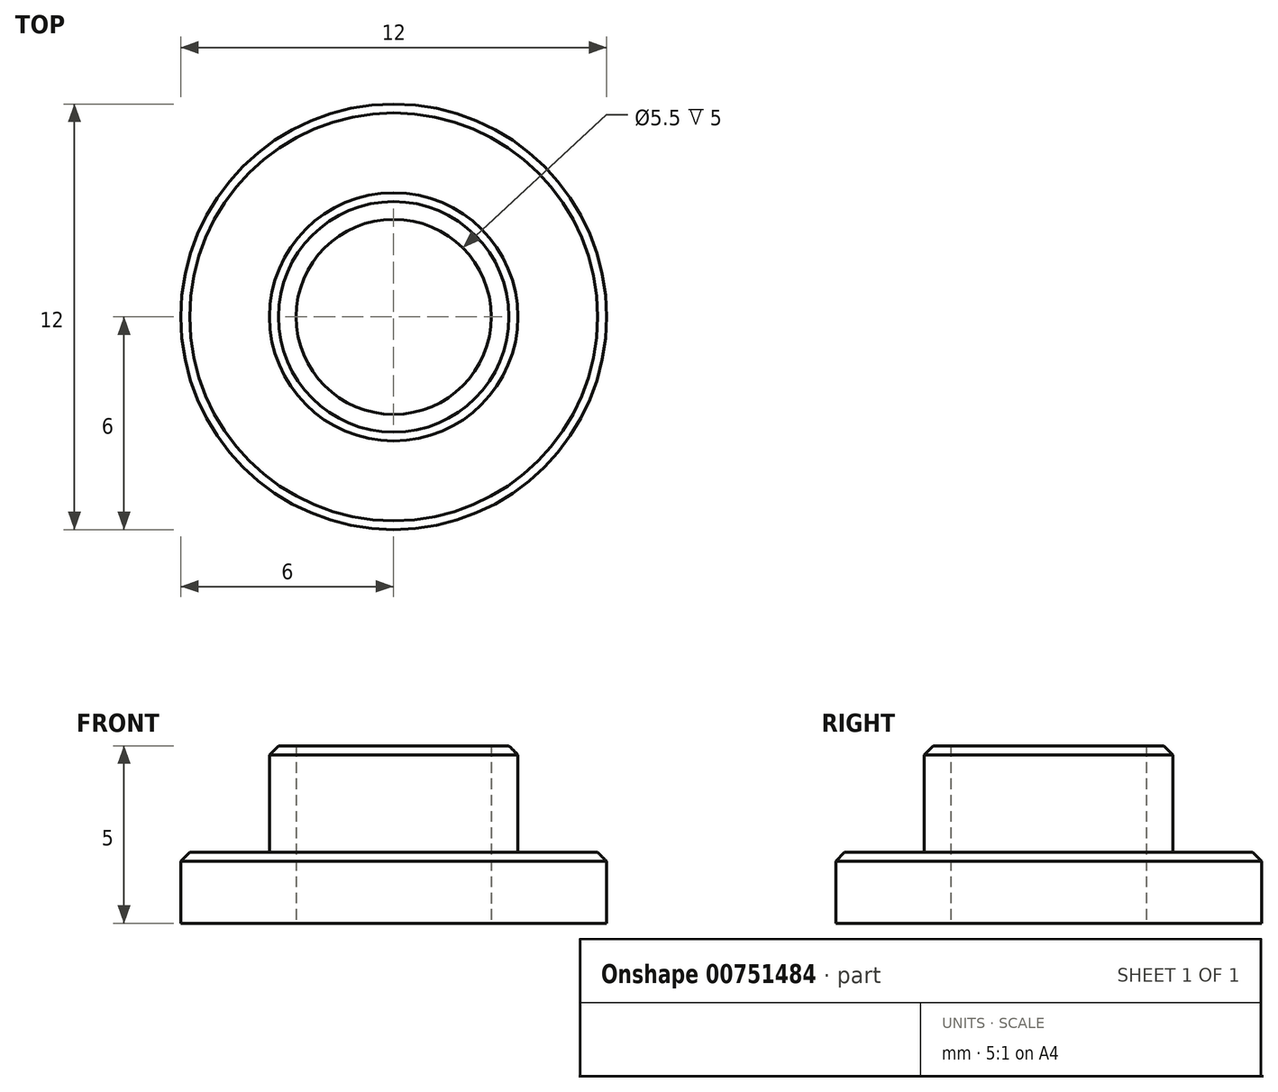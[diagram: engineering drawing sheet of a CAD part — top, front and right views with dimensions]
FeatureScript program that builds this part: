
annotation { "Feature Type Name" : "Feature", "Feature Type Description" : "" }
export const myFeature = defineFeature(function(context is Context, id is Id, definition is map)
    precondition{}
    {
        {
            assignVariable(context, id + "F0", {"name" : "SpacerHeight", "anyValue" : 5});
        }
        {
            var Q0;
            Q0=qCreatedBy(makeId("Top.planeOp"),FACE);
            var sketch = newSketch(context, id + "F1", { "sketchPlane" : qUnion([Q0])});
            skCircle(sketch, "E0", {"center": v(0, 0) * mm, "radius": 2.75 * mm});
            skCircle(sketch, "E1", {"center": v(0, 0) * mm, "radius": 3.5 * mm});
            skCircle(sketch, "E2", {"center": v(0, 0) * mm, "radius": 6 * mm});
            skSolve(sketch);
        }
        {
            var Q0;
            Q0=makeQuery(id+"F1.imprint","IMPRINT",FACE,{"disambiguationData":[TD([[makeQuery(id+"F1.imprint","IMPRINT",EDGE,{"derivedFrom":sQuery(id+"F1.wireOp",EDGE,"E0")}),-1.0]])]});
            extrude(context, id + "F2", {"entities" : qUnion([Q0]), "depth" : (getVariable(context, 'SpacerHeight')) * mm, "offsetDistance" : 25 * mm});
        }
        {
            var Q0;
            Q0=makeQuery(id+"F1.imprint","IMPRINT",FACE,{"disambiguationData":[TD([[makeQuery(id+"F1.imprint","IMPRINT",EDGE,{"derivedFrom":sQuery(id+"F1.wireOp",EDGE,"E1")}),-1.0]])]});
            extrude(context, id + "F3", {"entities" : qUnion([Q0]), "operationType" : NewBodyOperationType.ADD, "depth" : 2 * mm, "offsetDistance" : 25 * mm});
        }
        {
            var Q0;
            Q0=makeQuery(id+"F2.opExtrude","CAP_EDGE",EDGE,{"disambiguationData":[OSD([sQuery(id+"F1.wireOp",EDGE,"E1")])],"isStart":false});
            var Q1;
            Q1=makeQuery(id+"F2.opExtrude","CAP_EDGE",EDGE,{"disambiguationData":[OSD([sQuery(id+"F1.wireOp",EDGE,"E1")])],"isStart":true});
            var Q2;
            Q2=makeQuery(id+"F3.opExtrude","CAP_EDGE",EDGE,{"disambiguationData":[OSD([sQuery(id+"F1.wireOp",EDGE,"E1")])],"isStart":false});
            var Q3;
            Q3=makeQuery(id+"F3.opExtrude","CAP_EDGE",EDGE,{"disambiguationData":[OSD([sQuery(id+"F1.wireOp",EDGE,"E2")])],"isStart":false});
            chamfer(context, id + "F4", {"entities" : qUnion([Q0, Q1, Q2, Q3]), "width" : .25 * mm, "tangentPropagation" : true});
        }
    });
